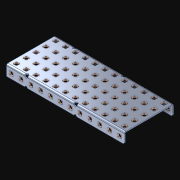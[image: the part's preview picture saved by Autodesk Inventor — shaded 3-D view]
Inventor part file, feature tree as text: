
AUTODESK INVENTOR PART (.ipt)
format: ipt  version: 2021 (Build 250183000, 183)  size: 1,724,416 bytes
history: native  units: in
note: dims shown in document units (in); Inventor stores cm internally (conversion verified against a paired STEP export)
features: extrude x85, other x85, sketch x4, pattern_linear x3
ambient origin geometry x8: Origin, YZ Plane, XZ Plane, XY Plane, X Axis, Y Axis, Z Axis, Center Point
bodies: Solid1 (feature_tree)
feature tree (177):
  pattern_linear  "Rectangular Pattern1"  Spacing1=0.182in  [1 undecoded]
  pattern_linear  "Rectangular Pattern2"  Spacing1=0.046in  [1 undecoded]
  pattern_linear  "Rectangular Pattern3"  Spacing1=0.5in  [1 undecoded]
  extrude  "Extrusion1"  Depth=0.046in
  sketch  "Sketch1"  dims[d0=0.182in]
  other  "Srf1"
  sketch  "Sketch2"  dims[d1=0.046in d2=0.0in]
  other  "Srf2"
  sketch  "Sketch3"  dims[d3=0.182in]
  other  "Srf3"
  other  "Srf4"
  other  "Srf5"
  other  "Srf6"
  other  "Srf7"
  other  "Srf8"
  other  "Srf9"
  other  "Srf10"
  other  "Srf11"
  other  "Srf12"
  other  "Srf13"
  other  "Srf14"
  other  "Srf38"
  other  "Srf39"
  other  "Srf40"
  other  "Srf41"
  other  "Srf42"
  other  "Srf43"
  other  "Srf44"
  other  "Srf45"
  other  "Srf46"
  other  "Srf47"
  other  "Srf48"
  other  "Srf72"
  other  "Srf73"
  other  "Srf74"
  other  "Srf75"
  other  "Srf76"
  other  "Srf77"
  other  "Srf78"
  other  "Srf79"
  other  "Srf80"
  other  "Srf81"
  other  "Srf82"
  other  "Srf83"
  other  "Srf107"
  other  "Srf108"
  other  "Srf109"
  other  "Srf110"
  other  "Srf111"
  other  "Srf112"
  other  "Srf113"
  other  "Srf114"
  other  "Srf115"
  other  "Srf116"
  other  "Srf117"
  other  "Srf118"
  other  "Srf142"
  other  "Srf143"
  other  "Srf144"
  other  "Srf145"
  other  "Srf146"
  other  "Srf147"
  other  "Srf148"
  other  "Srf149"
  other  "Srf150"
  other  "Srf151"
  other  "Srf152"
  other  "Srf153"
  other  "Srf177"
  other  "Srf178"
  other  "Srf179"
  other  "Srf180"
  other  "Srf181"
  other  "Srf182"
  other  "Srf183"
  other  "Srf184"
  other  "Srf185"
  other  "Srf186"
  other  "Srf187"
  other  "Srf188"
  other  "Srf212"
  other  "Srf213"
  other  "Srf214"
  other  "Srf215"
  other  "Srf216"
  other  "Srf217"
  other  "Srf218"
  other  "Srf219"
  other  "Srf220"
  other  "Srf221"
  other  "Srf222"
  sketch  "Sketch4"  dims[d4=0.046in d5=0.0in d6=0.182in d7=0.046in d8=0.0in d11=0.5in d12=4.7244in d14=0.5in d15=1.9685in d17=0.5in d18=4.7244in d20=0.5in d21=11.5in d22=0.0in]
  parser-record x1  (decoder bookkeeping rows leaked as tree rows — omitted from the tree; the rows remain in map.json)
  extrude  "ExtrusionSrf1"  Depth=0.046in
  extrude  "ExtrusionSrf2"  Depth=0.046in
  extrude  "ExtrusionSrf3"  Depth=0.046in
  extrude  "ExtrusionSrf4"  Depth=0.046in
  extrude  "ExtrusionSrf5"  Depth=0.046in
  extrude  "ExtrusionSrf6"  TaperAngle=0.0deg  [1 undecoded]
  extrude  "ExtrusionSrf7"  [1 undecoded]
  extrude  "ExtrusionSrf8"  [1 undecoded]
  extrude  "ExtrusionSrf9"  [1 undecoded]
  extrude  "ExtrusionSrf10"  [1 undecoded]
  extrude  "ExtrusionSrf11"  [1 undecoded]
  extrude  "ExtrusionSrf12"  [1 undecoded]
  extrude  "ExtrusionSrf13"  [1 undecoded]
  extrude  "ExtrusionSrf14"  [1 undecoded]
  extrude  "ExtrusionSrf38"  [1 undecoded]
  extrude  "ExtrusionSrf39"  [1 undecoded]
  extrude  "ExtrusionSrf40"  [1 undecoded]
  extrude  "ExtrusionSrf41"  [1 undecoded]
  extrude  "ExtrusionSrf42"  [1 undecoded]
  extrude  "ExtrusionSrf43"  [1 undecoded]
  extrude  "ExtrusionSrf44"  [1 undecoded]
  extrude  "ExtrusionSrf45"  [1 undecoded]
  extrude  "ExtrusionSrf46"  [1 undecoded]
  extrude  "ExtrusionSrf47"  [1 undecoded]
  extrude  "ExtrusionSrf48"  [1 undecoded]
  extrude  "ExtrusionSrf72"  [1 undecoded]
  extrude  "ExtrusionSrf73"  [1 undecoded]
  extrude  "ExtrusionSrf74"  [1 undecoded]
  extrude  "ExtrusionSrf75"  [1 undecoded]
  extrude  "ExtrusionSrf76"  [1 undecoded]
  extrude  "ExtrusionSrf77"  [1 undecoded]
  extrude  "ExtrusionSrf78"  [1 undecoded]
  extrude  "ExtrusionSrf79"  [1 undecoded]
  extrude  "ExtrusionSrf80"  [1 undecoded]
  extrude  "ExtrusionSrf81"  [1 undecoded]
  extrude  "ExtrusionSrf82"  [1 undecoded]
  extrude  "ExtrusionSrf83"  [1 undecoded]
  extrude  "ExtrusionSrf107"  [1 undecoded]
  extrude  "ExtrusionSrf108"  [1 undecoded]
  extrude  "ExtrusionSrf109"  [1 undecoded]
  extrude  "ExtrusionSrf110"  [1 undecoded]
  extrude  "ExtrusionSrf111"  [1 undecoded]
  extrude  "ExtrusionSrf112"  [1 undecoded]
  extrude  "ExtrusionSrf113"  [1 undecoded]
  extrude  "ExtrusionSrf114"  [1 undecoded]
  extrude  "ExtrusionSrf115"  [1 undecoded]
  extrude  "ExtrusionSrf116"  [1 undecoded]
  extrude  "ExtrusionSrf117"  [1 undecoded]
  extrude  "ExtrusionSrf118"  [1 undecoded]
  extrude  "ExtrusionSrf142"  [1 undecoded]
  extrude  "ExtrusionSrf143"  [1 undecoded]
  extrude  "ExtrusionSrf144"  [1 undecoded]
  extrude  "ExtrusionSrf145"  [1 undecoded]
  extrude  "ExtrusionSrf146"  [1 undecoded]
  extrude  "ExtrusionSrf147"  [1 undecoded]
  extrude  "ExtrusionSrf148"  [1 undecoded]
  extrude  "ExtrusionSrf149"  [1 undecoded]
  extrude  "ExtrusionSrf150"  [1 undecoded]
  extrude  "ExtrusionSrf151"  [1 undecoded]
  extrude  "ExtrusionSrf152"  [1 undecoded]
  extrude  "ExtrusionSrf153"  [1 undecoded]
  extrude  "ExtrusionSrf177"  [1 undecoded]
  extrude  "ExtrusionSrf178"  [1 undecoded]
  extrude  "ExtrusionSrf179"  [1 undecoded]
  extrude  "ExtrusionSrf180"  [1 undecoded]
  extrude  "ExtrusionSrf181"  [1 undecoded]
  extrude  "ExtrusionSrf182"  [1 undecoded]
  extrude  "ExtrusionSrf183"  [1 undecoded]
  extrude  "ExtrusionSrf184"  [1 undecoded]
  extrude  "ExtrusionSrf185"  [1 undecoded]
  extrude  "ExtrusionSrf186"  [1 undecoded]
  extrude  "ExtrusionSrf187"  [1 undecoded]
  extrude  "ExtrusionSrf188"  [1 undecoded]
  extrude  "ExtrusionSrf212"  [1 undecoded]
  extrude  "ExtrusionSrf213"  [1 undecoded]
  extrude  "ExtrusionSrf214"  [1 undecoded]
  extrude  "ExtrusionSrf215"  [1 undecoded]
  extrude  "ExtrusionSrf216"  [1 undecoded]
  extrude  "ExtrusionSrf217"  [1 undecoded]
  extrude  "ExtrusionSrf218"  [1 undecoded]
  extrude  "ExtrusionSrf219"  [1 undecoded]
  extrude  "ExtrusionSrf220"  [1 undecoded]
  extrude  "ExtrusionSrf221"  [1 undecoded]
  extrude  "ExtrusionSrf222"  [1 undecoded]
note: 82 required parameter values undecoded (feature->parameter linkage not recoverable at this tier; creation-order binding heuristic only, values carry confidence <= 0.55)
